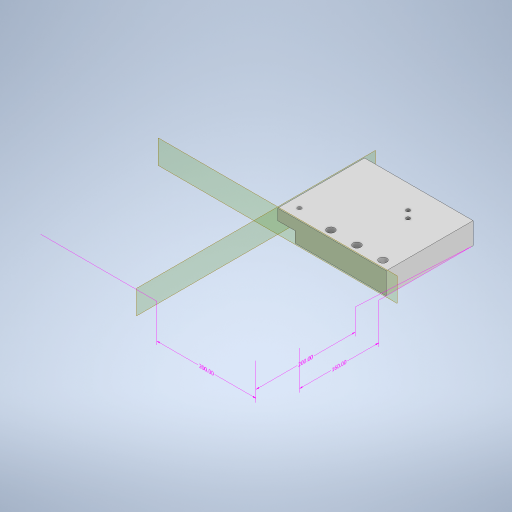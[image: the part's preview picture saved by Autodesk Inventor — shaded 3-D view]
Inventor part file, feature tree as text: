
AUTODESK INVENTOR PART (.ipt)
format: ipt  version: 2023 (Build 270158000, 158)  size: 371,200 bytes
history: native  units: mm
features: sketch x8, other x5, extrude x5, hole x3, plane x2, split x2
ambient origin geometry x8: Origin, YZ Plane, XZ Plane, XY Plane, X Axis, Y Axis, Z Axis, Center Point
bodies: Body1 (feature_tree)
feature tree (25):
  other  "Sólido1"
  other  "Anotaciones"
  extrude  "Extrusión1"  Depth=160.0mm
  extrude  "Extrusión2"  TaperAngle=0.0deg  [1 undecoded]
  extrude  "Extrusión3"  Depth=20.0mm TaperAngle=0.0deg
  extrude  "Extrusión4"  Depth=10.0mm
  hole  "Agujero1"  [1 undecoded]
  plane  "Plano de trabajo1"
  plane  "Plano de trabajo2"
  hole  "Agujero2"  [1 undecoded]
  extrude  "Extrusión5"  Depth=10.0mm
  hole  "Agujero3"  [1 undecoded]
  split  "Dividir1"
  split  "Dividir2"
  sketch  "Boceto1"  dims[d0=200.0mm d1=160.0mm]
  sketch  "Boceto2"  dims[d2=20.0mm d3=0.0mm]
  sketch  "Boceto3"  dims[d4=7.0mm d5=68.0mm d6=80.0mm d7=7.6mm d8=10.0mm d9=7.0mm d10=24.0mm d11=10.0mm d16=0.0mm]
  sketch  "Boceto4"  dims[d19=40.0mm d20=20.0mm d21=0.0mm]
  sketch  "Boceto5"  dims[d22=30.0mm d23=10.0mm]
  sketch  "Boceto6"  dims[d24=40.0mm d25=0.0mm d26=1.75mm]
  sketch  "Boceto7"  dims[d27=8.25mm d28=20.0mm]
  sketch  "Boceto8"  dims[d29=10.0mm d30=10.0mm d31=1.75mm d32=1.75mm d33=1.75mm d34=40.0mm d35=0.0mm d36=11.749873mm d37=40.0mm d38=29.999873mm d39=21.75mm d40=11.75mm d41=28.300341mm d42=11.749873mm d43=0.0mm d44=0.0mm d45=3.5mm d46=6.0mm d47=4.0mm d48=2.0mm d49=90.0deg d50=8.0mm d51=20.594885mm d58=30.0mm d59=30.0mm d63=3.5mm d64=10.0mm d65=10.0mm d66=3.5mm d67=6.0mm d68=4.0mm d69=2.0mm d70=90.0deg d71=8.0mm d72=20.594885mm d73=32.0mm d74=32.0mm d75=10.0mm d76=0.0mm d77=10.0mm d78=30.0mm d79=5.0mm d80=5.0mm d81=5.0mm d82=5.0mm d83=3.5mm d84=6.0mm d85=4.0mm d86=2.0mm d87=90.0deg d88=8.0mm d89=20.594885mm d52=6.692993mm d53=5.009025mm d54=200.0mm d55=6.065637mm d56=3.288093mm d57=200.0mm d60=3.204885mm d61=4.144173mm d62=160.0mm]
  other  "Cota lineal 1"
  other  "Cota lineal 2"
  other  "Cota lineal 3"
note: 4 required parameter values undecoded (feature->parameter linkage not recoverable at this tier; creation-order binding heuristic only, values carry confidence <= 0.55)
